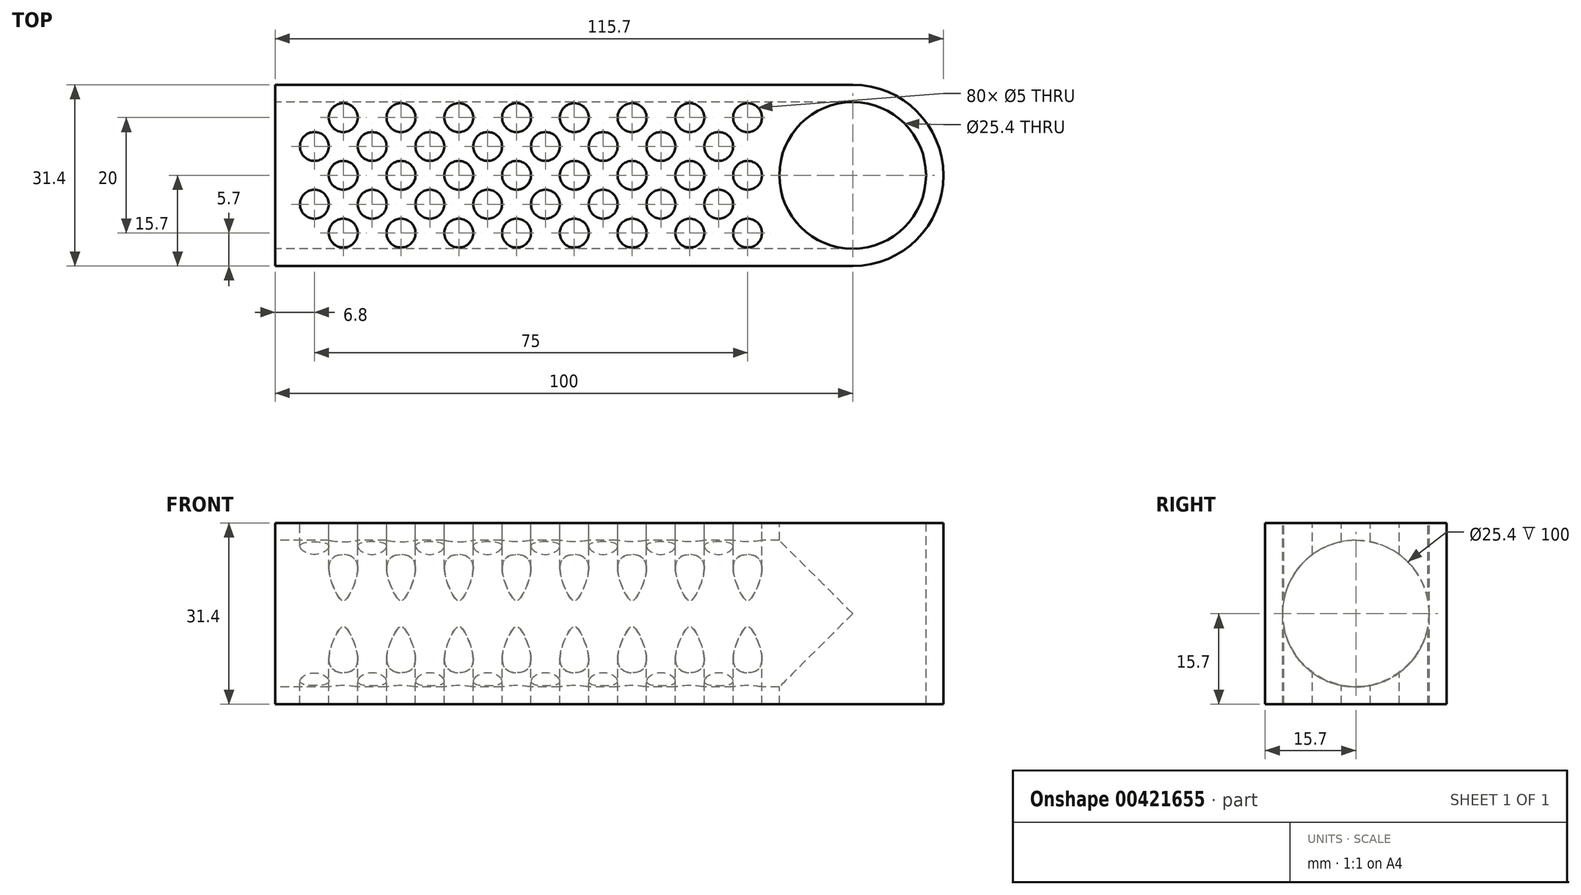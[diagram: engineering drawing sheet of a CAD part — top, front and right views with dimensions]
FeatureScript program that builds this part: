
annotation { "Feature Type Name" : "Feature", "Feature Type Description" : "" }
export const myFeature = defineFeature(function(context is Context, id is Id, definition is map)
    precondition{}
    {
        {
            var Q0;
            Q0=qCreatedBy(makeId("Top.planeOp"),FACE);
            var sketch = newSketch(context, id + "F0", { "sketchPlane" : qUnion([Q0])});
            skArc(sketch, "E0.0", {"start": v(0, -15.7) * mm, "mid": v(15.7, 0) * mm, "end": v(0, 15.7) * mm});
            skLineSegment(sketch, "E1", {"start": v(-100, 15.7) * mm, "end": v(-100, -15.7) * mm});
            skLineSegment(sketch, "E2", {"start": v(0, 15.7) * mm, "end": v(-100, 15.7) * mm});
            skLineSegment(sketch, "E3", {"start": v(0, -15.7) * mm, "end": v(-100, -15.7) * mm});
            skSolve(sketch);
        }
        {
            var Q0;
            Q0=makeQuery(id+"F0.imprint","IMPRINT",FACE,{"disambiguationData":[TD([[makeQuery(id+"F0.imprint","IMPRINT",EDGE,{"derivedFrom":sQuery(id+"F0.wireOp",EDGE,"E0.0")}),1.0]])]});
            extrude(context, id + "F1", {"entities" : qUnion([Q0]), "depth" : 31.4 * mm});
        }
        {
            var Q0;
            Q0=makeQuery(id+"F1.opExtrude","SWEPT_FACE",FACE,{"disambiguationData":[OSD([sQuery(id+"F0.wireOp",EDGE,"E1")])]});
            var sketch = newSketch(context, id + "F2", { "sketchPlane" : qUnion([Q0])});
            skCircle(sketch, "E4", {"center": v(0, 15.7) * mm, "radius": 12.7 * mm});
            skSolve(sketch);
        }
        {
            var Q0;
            Q0=makeQuery(id+"F1.opExtrude","CAP_FACE",FACE,{"disambiguationData":[OSD([sQuery(id+"F0.wireOp",EDGE,"E0.0"),sQuery(id+"F0.wireOp",EDGE,"E1"),sQuery(id+"F0.wireOp",EDGE,"E2"),sQuery(id+"F0.wireOp",EDGE,"E3")])],"isStart":false});
            var sketch = newSketch(context, id + "F3", { "sketchPlane" : qUnion([Q0])});
            skCircle(sketch, "E5", {"center": v(0, 0) * mm, "radius": 12.7 * mm});
            skSolve(sketch);
        }
        {
            var Q0;
            Q0 = qSketchRegion(id + "F3", true);
            extrude(context, id + "F4", {"entities" : qUnion([Q0]), "operationType" : NewBodyOperationType.REMOVE, "endBound" : BoundingType.THROUGH_ALL, "oppositeDirection" : true, "depth" : 25 * mm});
        }
        {
            var Q0;
            Q0 = qSketchRegion(id + "F2", true);
            extrude(context, id + "F5", {"entities" : qUnion([Q0]), "operationType" : NewBodyOperationType.REMOVE, "oppositeDirection" : true, "depth" : 100 * mm});
        }
        {
            var Q0;
            Q0=makeQuery(id+"F1.opExtrude","CAP_FACE",FACE,{"disambiguationData":[OSD([sQuery(id+"F0.wireOp",EDGE,"E0.0"),sQuery(id+"F0.wireOp",EDGE,"E1"),sQuery(id+"F0.wireOp",EDGE,"E2"),sQuery(id+"F0.wireOp",EDGE,"E3")])],"isStart":false});
            var sketch = newSketch(context, id + "F6", { "sketchPlane" : qUnion([Q0])});
            skCircle(sketch, "E6", {"center": v(-18.2, 0) * mm, "radius": 2.5 * mm});
            skCircle(sketch, "E7.1.0.0", {"center": v(-28.2, 0) * mm, "radius": 2.5 * mm});
            skCircle(sketch, "E7.2.0.0", {"center": v(-38.2, 0) * mm, "radius": 2.5 * mm});
            skCircle(sketch, "E7.3.0.0", {"center": v(-48.2, 0) * mm, "radius": 2.5 * mm});
            skCircle(sketch, "E7.4.0.0", {"center": v(-58.2, 0) * mm, "radius": 2.5 * mm});
            skCircle(sketch, "E7.5.0.0", {"center": v(-68.2, 0) * mm, "radius": 2.5 * mm});
            skCircle(sketch, "E7.6.0.0", {"center": v(-78.2, 0) * mm, "radius": 2.5 * mm});
            skCircle(sketch, "E7.7.0.0", {"center": v(-88.2, 0) * mm, "radius": 2.5 * mm});
            skCircle(sketch, "E8", {"center": v(-23.2, 5) * mm, "radius": 2.5 * mm});
            skCircle(sketch, "E9.1.0.0", {"center": v(-33.2, 5) * mm, "radius": 2.5 * mm});
            skCircle(sketch, "E9.2.0.0", {"center": v(-43.2, 5) * mm, "radius": 2.5 * mm});
            skCircle(sketch, "E9.3.0.0", {"center": v(-53.2, 5) * mm, "radius": 2.5 * mm});
            skCircle(sketch, "E9.4.0.0", {"center": v(-63.2, 5) * mm, "radius": 2.5 * mm});
            skCircle(sketch, "E9.5.0.0", {"center": v(-73.2, 5) * mm, "radius": 2.5 * mm});
            skCircle(sketch, "E9.6.0.0", {"center": v(-83.2, 5) * mm, "radius": 2.5 * mm});
            skCircle(sketch, "E9.7.0.0", {"center": v(-93.2, 5) * mm, "radius": 2.5 * mm});
            skCircle(sketch, "E10.MirrorC", {"center": v(-93.2, -5) * mm, "radius": 2.5 * mm});
            skCircle(sketch, "E11.MirrorC", {"center": v(-83.2, -5) * mm, "radius": 2.5 * mm});
            skCircle(sketch, "E12.MirrorC", {"center": v(-73.2, -5) * mm, "radius": 2.5 * mm});
            skCircle(sketch, "E13.MirrorC", {"center": v(-63.2, -5) * mm, "radius": 2.5 * mm});
            skCircle(sketch, "E14.MirrorC", {"center": v(-53.2, -5) * mm, "radius": 2.5 * mm});
            skCircle(sketch, "E15.MirrorC", {"center": v(-43.2, -5) * mm, "radius": 2.5 * mm});
            skCircle(sketch, "E16.MirrorC", {"center": v(-33.2, -5) * mm, "radius": 2.5 * mm});
            skCircle(sketch, "E17.MirrorC", {"center": v(-23.2, -5) * mm, "radius": 2.5 * mm});
            skCircle(sketch, "E18.MirrorC", {"center": v(-88.2, 10) * mm, "radius": 2.5 * mm});
            skCircle(sketch, "E19.MirrorC", {"center": v(-78.2, 10) * mm, "radius": 2.5 * mm});
            skCircle(sketch, "E20.MirrorC", {"center": v(-68.2, 10) * mm, "radius": 2.5 * mm});
            skCircle(sketch, "E21.MirrorC", {"center": v(-58.2, 10) * mm, "radius": 2.5 * mm});
            skCircle(sketch, "E22.MirrorC", {"center": v(-48.2, 10) * mm, "radius": 2.5 * mm});
            skCircle(sketch, "E23.MirrorC", {"center": v(-38.2, 10) * mm, "radius": 2.5 * mm});
            skCircle(sketch, "E24.MirrorC", {"center": v(-28.2, 10) * mm, "radius": 2.5 * mm});
            skCircle(sketch, "E25.MirrorC", {"center": v(-18.2, 10) * mm, "radius": 2.5 * mm});
            skCircle(sketch, "E26.MirrorC", {"center": v(-88.2, -10) * mm, "radius": 2.5 * mm});
            skCircle(sketch, "E27.MirrorC", {"center": v(-78.2, -10) * mm, "radius": 2.5 * mm});
            skCircle(sketch, "E28.MirrorC", {"center": v(-68.2, -10) * mm, "radius": 2.5 * mm});
            skCircle(sketch, "E29.MirrorC", {"center": v(-58.2, -10) * mm, "radius": 2.5 * mm});
            skCircle(sketch, "E30.MirrorC", {"center": v(-48.2, -10) * mm, "radius": 2.5 * mm});
            skCircle(sketch, "E31.MirrorC", {"center": v(-38.2, -10) * mm, "radius": 2.5 * mm});
            skCircle(sketch, "E32.MirrorC", {"center": v(-28.2, -10) * mm, "radius": 2.5 * mm});
            skCircle(sketch, "E33.MirrorC", {"center": v(-18.2, -10) * mm, "radius": 2.5 * mm});
            skSolve(sketch);
        }
        {
            var Q0;
            Q0 = qSketchRegion(id + "F6", true);
            extrude(context, id + "F7", {"entities" : qUnion([Q0]), "operationType" : NewBodyOperationType.REMOVE, "endBound" : BoundingType.THROUGH_ALL, "oppositeDirection" : true, "depth" : 25 * mm});
        }
    });
